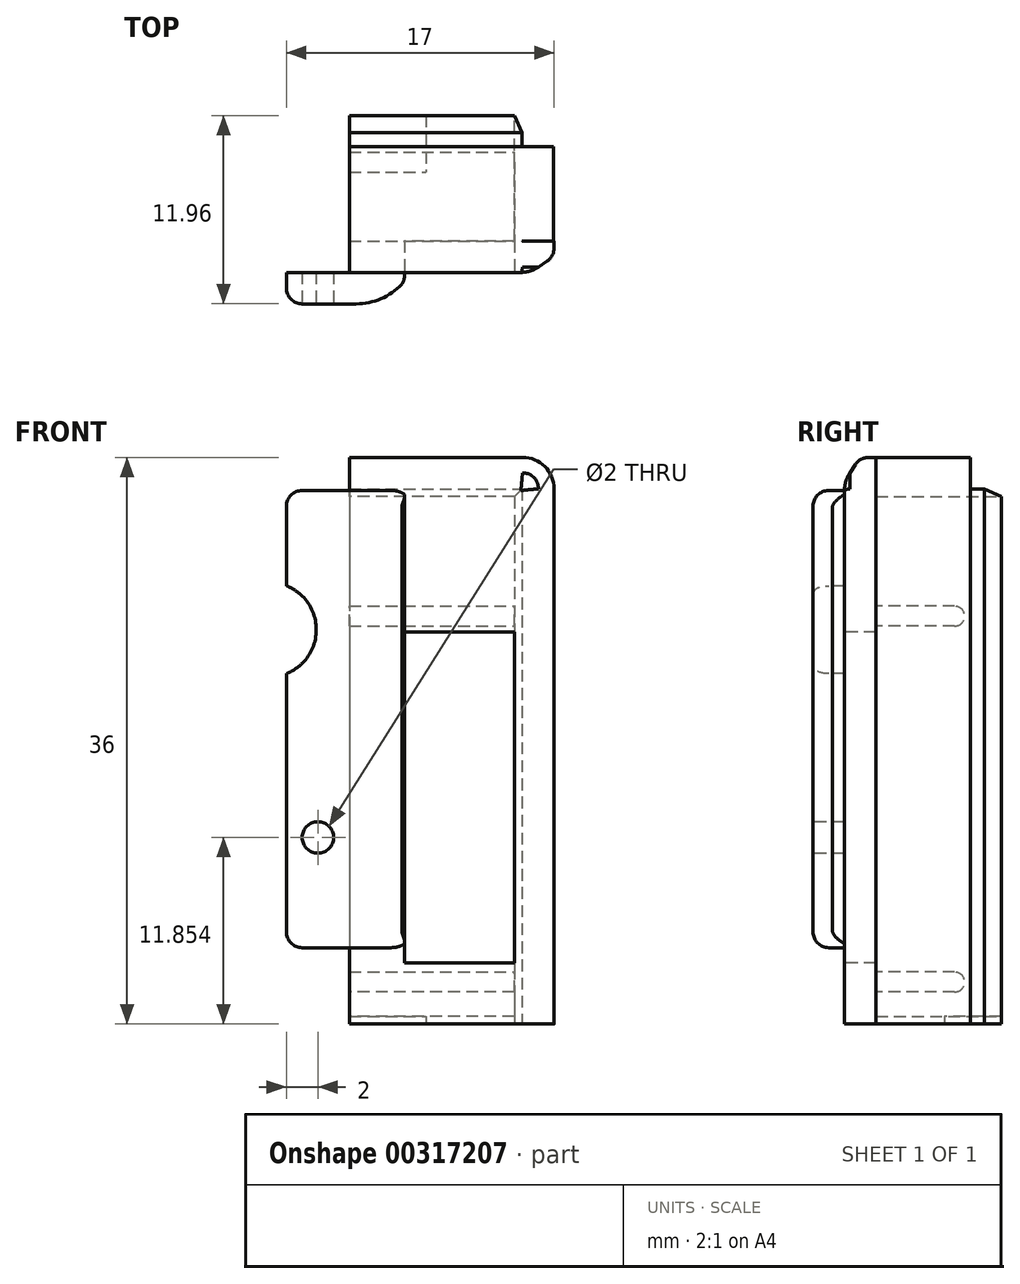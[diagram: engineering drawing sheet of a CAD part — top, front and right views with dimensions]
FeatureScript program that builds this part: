
annotation { "Feature Type Name" : "Feature", "Feature Type Description" : "" }
export const myFeature = defineFeature(function(context is Context, id is Id, definition is map)
    precondition{}
    {
        {
            var Q0;
            Q0=qCreatedBy(makeId("Front.planeOp"),FACE);
            var sketch = newSketch(context, id + "F0", { "sketchPlane" : qUnion([Q0])});
            skLineSegment(sketch, "E0", {"start": v(12.98, 36.3) * mm, "end": v(12.98, 70.29) * mm});
            skLineSegment(sketch, "E1", {"start": v(10.98, 72.29) * mm, "end": v(0, 72.29) * mm});
            skLineSegment(sketch, "E2", {"start": v(0, 72.29) * mm, "end": v(0, 70.29) * mm});
            skLineSegment(sketch, "E3", {"start": v(0, 70.29) * mm, "end": v(10.98, 70.29) * mm});
            skLineSegment(sketch, "E4", {"start": v(10.98, 70.29) * mm, "end": v(10.98, 36.3) * mm});
            skPoint(sketch, "E5.visualSharp", {"position": v(12.98, 72.29) * mm});
            skArc(sketch, "E5.filletArc", {"start": v(12.98, 70.29) * mm, "mid": v(12.4, 71.7) * mm, "end": v(10.98, 72.29) * mm});
            skPoint(sketch, "E6.visualSharp", {"position": v(12.98, 0) * mm});
            skLineSegment(sketch, "E7", {"start": v(10.98, 36.3) * mm, "end": v(12.98, 36.3) * mm});
            skPoint(sketch, "E8.start.orphan", {"position": v(0, 2) * mm});
            skSolve(sketch);
        }
        {
            var Q0;
            Q0=makeQuery(id+"F0.imprint","IMPRINT",FACE,{"disambiguationData":[TD([[makeQuery(id+"F0.imprint","IMPRINT",EDGE,{"derivedFrom":sQuery(id+"F0.wireOp",EDGE,"E0")}),1.0]])]});
            extrude(context, id + "F1", {"entities" : qUnion([Q0]), "depth" : 6 * mm});
        }
        {
            var Q0;
            Q0=makeQuery(id+"F1.opExtrude","SWEPT_FACE",FACE,{"disambiguationData":[OSD([sQuery(id+"F0.wireOp",EDGE,"E2")])]});
            var sketch = newSketch(context, id + "F2", { "sketchPlane" : qUnion([Q0])});
            skLineSegment(sketch, "E9.bottom", {"start": v(6, 72.29) * mm, "end": v(8, 72.29) * mm});
            skLineSegment(sketch, "E9.top", {"start": v(6, 36.3) * mm, "end": v(8, 36.3) * mm});
            skLineSegment(sketch, "E9.left", {"start": v(6, 72.29) * mm, "end": v(6, 36.3) * mm});
            skLineSegment(sketch, "E9.right", {"start": v(8, 72.29) * mm, "end": v(8, 36.3) * mm});
            skSolve(sketch);
        }
        {
            var Q0;
            Q0=qSketchRegion(id+"F2",true);
            extrude(context, id + "F3", {"entities" : qUnion([Q0]), "operationType" : NewBodyOperationType.ADD, "oppositeDirection" : true, "depth" : 13 * mm});
        }
        {
            var Q0;
            Q0=makeQuery(id+"F3.opExtrude","CAP_EDGE",EDGE,{"disambiguationData":[OSD([sQuery(id+"F2.wireOp",EDGE,"E9.bottom")])],"isStart":false});
            fillet(context, id + "F4", {"entities" : qUnion([Q0]), "radius" : 2 * mm, "tangentPropagation" : true, "allowEdgeOverflow" : false});
        }
        {
            var Q0;
            Q0=makeQuery(id+"F3.opExtrude","SWEPT_FACE",FACE,{"disambiguationData":[OSD([sQuery(id+"F2.wireOp",EDGE,"E9.right")])]});
            var sketch = newSketch(context, id + "F5", { "sketchPlane" : qUnion([Q0])});
            skLineSegment(sketch, "E10.bottom", {"start": v(3.5, 70.18) * mm, "end": v(-4, 70.18) * mm});
            skLineSegment(sketch, "E10.top", {"start": v(3.5, 41.14) * mm, "end": v(-4, 41.14) * mm});
            skLineSegment(sketch, "E10.left", {"start": v(3.5, 70.18) * mm, "end": v(3.5, 41.14) * mm});
            skLineSegment(sketch, "E10.right", {"start": v(-4, 70.18) * mm, "end": v(-4, 41.14) * mm});
            skSolve(sketch);
        }
        {
            var Q0;
            Q0=qSketchRegion(id+"F5",true);
            extrude(context, id + "F6", {"entities" : qUnion([Q0]), "operationType" : NewBodyOperationType.ADD, "depth" : 2 * mm});
        }
        {
            var Q0;
            Q0=makeQuery(id+"F6.opExtrude","CAP_EDGE",EDGE,{"disambiguationData":[OSD([sQuery(id+"F5.wireOp",EDGE,"E10.left")])],"isStart":false});
            chamfer(context, id + "F7", {"entities" : qUnion([Q0]), "chamferType" : ChamferType.TWO_OFFSETS, "width1" : 1.5 * mm, "oppositeDirection" : false, "width2" : 1 * mm, "tangentPropagation" : true});
        }
        {
            var Q0;
            {var subQ0=sQuery(id+"F5.wireOp",EDGE,"E10.left");Q0=makeQuery(id+"F7.opChamfer","BLEND_EDGE",EDGE,{"blendedFrom":[makeQuery(id+"F6.opExtrude","CAP_EDGE",EDGE,{"disambiguationData":[OSD([subQ0])],"isStart":false}),makeQuery(id+"F6.opExtrude","SWEPT_FACE",FACE,{"disambiguationData":[OSD([subQ0])]})],"blendedInto":[makeQuery(id+"F6.opExtrude","SWEPT_FACE",FACE,{"disambiguationData":[OSD([subQ0])]})]});}
            fillet(context, id + "F8", {"entities" : qUnion([Q0]), "radius" : 1 * mm, "tangentPropagation" : true, "allowEdgeOverflow" : false});
        }
        {
            var Q0;
            Q0=makeQuery(id+"F6.opExtrude","CAP_FACE",FACE,{"disambiguationData":[OSD([sQuery(id+"F5.wireOp",EDGE,"E10.bottom"),sQuery(id+"F5.wireOp",EDGE,"E10.top"),sQuery(id+"F5.wireOp",EDGE,"E10.left"),sQuery(id+"F5.wireOp",EDGE,"E10.right")])],"isStart":false});
            var sketch = newSketch(context, id + "F9", { "sketchPlane" : qUnion([Q0])});
            skCircle(sketch, "E11", {"center": v(-2, 48.14) * mm, "radius": 1 * mm});
            skSolve(sketch);
        }
        {
            var Q0;
            Q0=qSketchRegion(id+"F9",true);
            extrude(context, id + "F10", {"entities" : qUnion([Q0]), "operationType" : NewBodyOperationType.REMOVE, "oppositeDirection" : true, "depth" : 25 * mm});
        }
        {
            var Q0;
            Q0=makeQuery(id+"F3.opExtrude","SWEPT_EDGE",EDGE,{"disambiguationData":[OSD([sQuery(id+"F2.wireOp",EDGE,"E9.bottom"),sQuery(id+"F2.wireOp",EDGE,"E9.right")])]});
            chamfer(context, id + "F11", {"entities" : qUnion([Q0]), "chamferType" : ChamferType.TWO_OFFSETS, "width1" : 1.5 * mm, "oppositeDirection" : false, "width2" : 1 * mm, "tangentPropagation" : true});
        }
        {
            var Q0;
            {var subQ0=sQuery(id+"F2.wireOp",EDGE,"E9.bottom");Q0=makeQuery(id+"F11.opChamfer","BLEND_EDGE",EDGE,{"blendedFrom":[makeQuery(id+"F3.opExtrude","SWEPT_EDGE",EDGE,{"disambiguationData":[OSD([subQ0,sQuery(id+"F2.wireOp",EDGE,"E9.right")])]}),makeQuery(id+"F3.boolean.opBoolean","MERGE",FACE,{"derivedFrom":[makeQuery(id+"F1.opExtrude","SWEPT_FACE",FACE,{"disambiguationData":[OSD([sQuery(id+"F0.wireOp",EDGE,"E1")])]}),makeQuery(id+"F3.opExtrude","SWEPT_FACE",FACE,{"disambiguationData":[OSD([subQ0])]})]})],"blendedInto":[makeQuery(id+"F3.boolean.opBoolean","MERGE",FACE,{"derivedFrom":[makeQuery(id+"F1.opExtrude","SWEPT_FACE",FACE,{"disambiguationData":[OSD([sQuery(id+"F0.wireOp",EDGE,"E1")])]}),makeQuery(id+"F3.opExtrude","SWEPT_FACE",FACE,{"disambiguationData":[OSD([subQ0])]})]})]});}
            fillet(context, id + "F12", {"entities" : qUnion([Q0]), "radius" : 1 * mm, "tangentPropagation" : true, "allowEdgeOverflow" : false});
        }
        {
            var Q0;
            {var subQ0=sQuery(id+"F2.wireOp",EDGE,"E9.right");Q0=makeQuery(id+"F11.opChamfer","BLEND_EDGE",EDGE,{"blendedFrom":[makeQuery(id+"F3.opExtrude","SWEPT_EDGE",EDGE,{"disambiguationData":[OSD([sQuery(id+"F2.wireOp",EDGE,"E9.bottom"),subQ0])]}),makeQuery(id+"F3.opExtrude","SWEPT_FACE",FACE,{"disambiguationData":[OSD([subQ0])]})],"blendedInto":[makeQuery(id+"F3.opExtrude","SWEPT_FACE",FACE,{"disambiguationData":[OSD([subQ0])]})]});}
            fillet(context, id + "F13", {"entities" : qUnion([Q0]), "radius" : 2 * mm, "tangentPropagation" : true, "allowEdgeOverflow" : false});
        }
        {
            var Q0;
            {var subQ0=sQuery(id+"F5.wireOp",EDGE,"E10.left");Q0=makeQuery(id+"F7.opChamfer","BLEND_EDGE",EDGE,{"blendedFrom":[makeQuery(id+"F6.opExtrude","CAP_EDGE",EDGE,{"disambiguationData":[OSD([subQ0])],"isStart":false}),makeQuery(id+"F6.opExtrude","CAP_FACE",FACE,{"disambiguationData":[OSD([sQuery(id+"F5.wireOp",EDGE,"E10.bottom"),sQuery(id+"F5.wireOp",EDGE,"E10.top"),subQ0,sQuery(id+"F5.wireOp",EDGE,"E10.right")])],"isStart":false})],"blendedInto":[makeQuery(id+"F6.opExtrude","CAP_FACE",FACE,{"disambiguationData":[OSD([sQuery(id+"F5.wireOp",EDGE,"E10.bottom"),sQuery(id+"F5.wireOp",EDGE,"E10.top"),subQ0,sQuery(id+"F5.wireOp",EDGE,"E10.right")])],"isStart":false})]});}
            fillet(context, id + "F14", {"entities" : qUnion([Q0]), "radius" : 4 * mm, "tangentPropagation" : true, "allowEdgeOverflow" : false});
        }
        {
            var Q0;
            Q0=makeQuery(id+"F6.opExtrude","CAP_EDGE",EDGE,{"disambiguationData":[OSD([sQuery(id+"F5.wireOp",EDGE,"E10.top")])],"isStart":false});
            var Q1;
            Q1=makeQuery(id+"F6.opExtrude","CAP_EDGE",EDGE,{"disambiguationData":[OSD([sQuery(id+"F5.wireOp",EDGE,"E10.bottom")])],"isStart":false});
            fillet(context, id + "F15", {"entities" : qUnion([Q0, Q1]), "radius" : 1 * mm, "tangentPropagation" : true, "allowEdgeOverflow" : false});
        }
        {
            var Q0;
            Q0=makeQuery(id+"F6.opExtrude","CAP_EDGE",EDGE,{"disambiguationData":[OSD([sQuery(id+"F5.wireOp",EDGE,"E10.right")])],"isStart":false});
            fillet(context, id + "F16", {"entities" : qUnion([Q0]), "radius" : 1 * mm, "tangentPropagation" : true, "allowEdgeOverflow" : false});
        }
        {
            var Q0;
            Q0=makeQuery(id+"F1.opExtrude","CAP_FACE",FACE,{"disambiguationData":[OSD([sQuery(id+"F0.wireOp",EDGE,"E0"),sQuery(id+"F0.wireOp",EDGE,"E1"),sQuery(id+"F0.wireOp",EDGE,"E2"),sQuery(id+"F0.wireOp",EDGE,"E3"),sQuery(id+"F0.wireOp",EDGE,"E4"),sQuery(id+"F0.wireOp",EDGE,"E5.filletArc"),sQuery(id+"F0.wireOp",EDGE,"E7")])],"isStart":true});
            var sketch = newSketch(context, id + "F17", { "sketchPlane" : qUnion([Q0])});
            skLineSegment(sketch, "E12.bottom", {"start": v(-10.98, 70.29) * mm, "end": v(-10.48, 70.29) * mm});
            skLineSegment(sketch, "E12.top", {"start": v(-10.98, 36.3) * mm, "end": v(-10.48, 36.3) * mm});
            skLineSegment(sketch, "E12.left", {"start": v(-10.98, 70.29) * mm, "end": v(-10.98, 36.3) * mm});
            skLineSegment(sketch, "E12.right", {"start": v(-10.48, 70.29) * mm, "end": v(-10.48, 36.3) * mm});
            skLineSegment(sketch, "E13.bottom", {"start": v(-10.98, 70.29) * mm, "end": v(0, 70.29) * mm});
            skLineSegment(sketch, "E13.top", {"start": v(-10.98, 69.79) * mm, "end": v(0, 69.79) * mm});
            skLineSegment(sketch, "E13.left", {"start": v(-10.98, 70.29) * mm, "end": v(-10.98, 69.79) * mm});
            skLineSegment(sketch, "E13.right", {"start": v(0, 70.29) * mm, "end": v(0, 69.79) * mm});
            skLineSegment(sketch, "E14.bottom", {"start": v(-10.98, 36.3) * mm, "end": v(0, 36.3) * mm});
            skLineSegment(sketch, "E14.top", {"start": v(-10.98, 36.8) * mm, "end": v(0, 36.8) * mm});
            skLineSegment(sketch, "E14.left", {"start": v(-10.98, 36.3) * mm, "end": v(-10.98, 36.8) * mm});
            skLineSegment(sketch, "E14.right", {"start": v(0, 36.3) * mm, "end": v(0, 36.8) * mm});
            skSolve(sketch);
        }
        {
            var Q0;
            Q0=qSketchRegion(id+"F17",true);
            extrude(context, id + "F18", {"entities" : qUnion([Q0]), "operationType" : NewBodyOperationType.ADD, "oppositeDirection" : true, "depth" : 6.1 * mm, "hasSecondDirection" : true, "secondDirectionOppositeDirection" : false, "secondDirectionDepth" : 1.97 * mm});
        }
        {
            var Q0;
            Q0=makeQuery(id+"F18.opExtrude","CAP_EDGE",EDGE,{"disambiguationData":[OSD([sQuery(id+"F17.wireOp",EDGE,"E12.left"),sQuery(id+"F17.wireOp",EDGE,"E13.left")])],"isStart":true});
            var Q1;
            Q1=makeQuery(id+"F18.opExtrude","CAP_EDGE",EDGE,{"disambiguationData":[OSD([sQuery(id+"F17.wireOp",EDGE,"E13.bottom")])],"isStart":true});
            chamfer(context, id + "F19", {"entities" : qUnion([Q0, Q1]), "chamferType" : ChamferType.OFFSET_ANGLE, "width" : 0.5 * mm, "oppositeDirection" : false, "angle" : 65 * degree, "tangentPropagation" : true});
        }
        {
            var Q0;
            Q0=makeQuery(id+"F18.boolean.opBoolean","MERGE",FACE,{"derivedFrom":[makeQuery(id+"F3.boolean.opBoolean","MERGE",FACE,{"derivedFrom":[makeQuery(id+"F1.opExtrude","SWEPT_FACE",FACE,{"disambiguationData":[OSD([sQuery(id+"F0.wireOp",EDGE,"E7")])]}),makeQuery(id+"F3.opExtrude","SWEPT_FACE",FACE,{"disambiguationData":[OSD([sQuery(id+"F2.wireOp",EDGE,"E9.top")])]})]}),makeQuery(id+"F18.opExtrude","SWEPT_FACE",FACE,{"disambiguationData":[OSD([sQuery(id+"F17.wireOp",EDGE,"E14.bottom")])]})]});
            var sketch = newSketch(context, id + "F20", { "sketchPlane" : qUnion([Q0])});
            skLineSegment(sketch, "E15.bottom", {"start": v(0, -1.97) * mm, "end": v(4.88, -1.97) * mm});
            skLineSegment(sketch, "E15.top", {"start": v(0, 1.64) * mm, "end": v(4.88, 1.64) * mm});
            skLineSegment(sketch, "E15.left", {"start": v(0, -1.97) * mm, "end": v(0, 1.64) * mm});
            skLineSegment(sketch, "E15.right", {"start": v(4.88, -1.97) * mm, "end": v(4.88, 1.64) * mm});
            skSolve(sketch);
        }
        {
            var Q0;
            Q0=makeQuery(id+"F20.imprint","IMPRINT",FACE,{"disambiguationData":[TD([[makeQuery(id+"F20.imprint","IMPRINT",EDGE,{"derivedFrom":sQuery(id+"F20.wireOp",EDGE,"E15.bottom")}),-1.0]])]});
            extrude(context, id + "F21", {"entities" : qUnion([Q0]), "operationType" : NewBodyOperationType.REMOVE, "oppositeDirection" : true, "depth" : 3.3 * mm});
        }
        {
            var Q0;
            {var subQ1=sQuery(id+"F2.wireOp",EDGE,"E9.left");Q0=makeQuery(id+"F3.boolean.opBoolean","SPLIT",FACE,{"disambiguationData":[TD([makeQuery(id+"F1.opExtrude","SWEPT_FACE",FACE,{"disambiguationData":[OSD([sQuery(id+"F0.wireOp",EDGE,"E2")])]})])],"derivedFrom":makeQuery(id+"F3.opExtrude","SWEPT_FACE",FACE,{"disambiguationData":[OSD([subQ1])]})});}
            var sketch = newSketch(context, id + "F22", { "sketchPlane" : qUnion([Q0])});
            skLineSegment(sketch, "E16", {"start": v(-10.48, 38.33) * mm, "end": v(-7.39, 38.33) * mm});
            skLineSegment(sketch, "E17", {"start": v(-10.48, 39.6) * mm, "end": v(-7.39, 39.6) * mm});
            skLineSegment(sketch, "E18", {"start": v(-7.39, 38.33) * mm, "end": v(0, 38.33) * mm});
            skLineSegment(sketch, "E19", {"start": v(0, 38.33) * mm, "end": v(0, 39.6) * mm});
            skLineSegment(sketch, "E20", {"start": v(0, 39.6) * mm, "end": v(-7.39, 39.6) * mm});
            skLineSegment(sketch, "E21.bottom", {"start": v(0, 62.84) * mm, "end": v(-10.48, 62.84) * mm});
            skLineSegment(sketch, "E21.top", {"start": v(0, 61.57) * mm, "end": v(-10.48, 61.57) * mm});
            skLineSegment(sketch, "E21.left", {"start": v(0, 62.84) * mm, "end": v(0, 61.57) * mm});
            skLineSegment(sketch, "E21.right", {"start": v(-10.48, 62.84) * mm, "end": v(-10.48, 61.57) * mm});
            skSolve(sketch);
        }
        {
            var Q0;
            {var subQ0=sQuery(id+"F22.wireOp",EDGE,"E16");Q0=makeQuery(id+"F22.imprint","IMPRINT",FACE,{"disambiguationData":[TD([[makeQuery(id+"F22.imprint","IMPRINT",EDGE,{"derivedFrom":subQ0}),1.0]])]});}
            var Q1;
            Q1=makeQuery(id+"F22.imprint","IMPRINT",FACE,{"disambiguationData":[TD([[makeQuery(id+"F22.imprint","IMPRINT",EDGE,{"derivedFrom":sQuery(id+"F22.wireOp",EDGE,"E21.bottom")}),1.0]])]});
            extrude(context, id + "F23", {"entities" : qUnion([Q0, Q1]), "operationType" : NewBodyOperationType.ADD, "depth" : 5.63 * mm});
        }
        {
            var Q0;
            Q0=makeQuery(id+"F23.opExtrude","CAP_EDGE",EDGE,{"disambiguationData":[OSD([sQuery(id+"F22.wireOp",EDGE,"E16")])],"isStart":false});
            var Q1;
            Q1=makeQuery(id+"F23.opExtrude","CAP_EDGE",EDGE,{"disambiguationData":[OSD([sQuery(id+"F22.wireOp",EDGE,"E17")])],"isStart":false});
            var Q2;
            Q2=makeQuery(id+"F23.opExtrude","CAP_EDGE",EDGE,{"disambiguationData":[OSD([sQuery(id+"F22.wireOp",EDGE,"E21.top")])],"isStart":false});
            var Q3;
            Q3=makeQuery(id+"F23.opExtrude","CAP_EDGE",EDGE,{"disambiguationData":[OSD([sQuery(id+"F22.wireOp",EDGE,"E21.bottom")])],"isStart":false});
            fillet(context, id + "F24", {"entities" : qUnion([Q0, Q1, Q2, Q3]), "radius" : 0.64 * mm, "tangentPropagation" : true, "allowEdgeOverflow" : false});
        }
        {
            var Q0;
            Q0=makeQuery(id+"F3.opExtrude","SWEPT_FACE",FACE,{"disambiguationData":[OSD([sQuery(id+"F2.wireOp",EDGE,"E9.right")])]});
            var sketch = newSketch(context, id + "F25", { "sketchPlane" : qUnion([Q0])});
            skLineSegment(sketch, "E22.bottom", {"start": v(3.5, 61.18) * mm, "end": v(10.48, 61.18) * mm});
            skLineSegment(sketch, "E22.top", {"start": v(3.5, 40.18) * mm, "end": v(10.48, 40.18) * mm});
            skLineSegment(sketch, "E22.left", {"start": v(3.5, 61.18) * mm, "end": v(3.5, 40.18) * mm});
            skLineSegment(sketch, "E22.right", {"start": v(10.48, 61.18) * mm, "end": v(10.48, 40.18) * mm});
            skSolve(sketch);
        }
        {
            var Q0;
            Q0=makeQuery(id+"F25.imprint","IMPRINT",FACE,{"disambiguationData":[TD([[makeQuery(id+"F25.imprint","IMPRINT",EDGE,{"derivedFrom":sQuery(id+"F25.wireOp",EDGE,"E22.bottom")}),-1.0]])]});
            extrude(context, id + "F26", {"entities" : qUnion([Q0]), "operationType" : NewBodyOperationType.REMOVE, "oppositeDirection" : true, "depth" : 25 * mm});
        }
        {
            var Q0;
            Q0=makeQuery(id+"F16.opFillet","SPLIT",FACE,{"disambiguationData":[OD(1.0)],"derivedFrom":makeQuery(id+"F6.opExtrude","CAP_FACE",FACE,{"disambiguationData":[OSD([sQuery(id+"F5.wireOp",EDGE,"E10.bottom"),sQuery(id+"F5.wireOp",EDGE,"E10.top"),sQuery(id+"F5.wireOp",EDGE,"E10.left"),sQuery(id+"F5.wireOp",EDGE,"E10.right")])],"isStart":false})});
            var sketch = newSketch(context, id + "F27", { "sketchPlane" : qUnion([Q0])});
            skCircle(sketch, "E23", {"center": v(-5.1, 61.34) * mm, "radius": 3 * mm});
            skSolve(sketch);
        }
        {
            var Q0;
            Q0=qSketchRegion(id+"F27",true);
            extrude(context, id + "F28", {"entities" : qUnion([Q0]), "operationType" : NewBodyOperationType.REMOVE, "oppositeDirection" : true, "depth" : 25 * mm});
        }
    });
